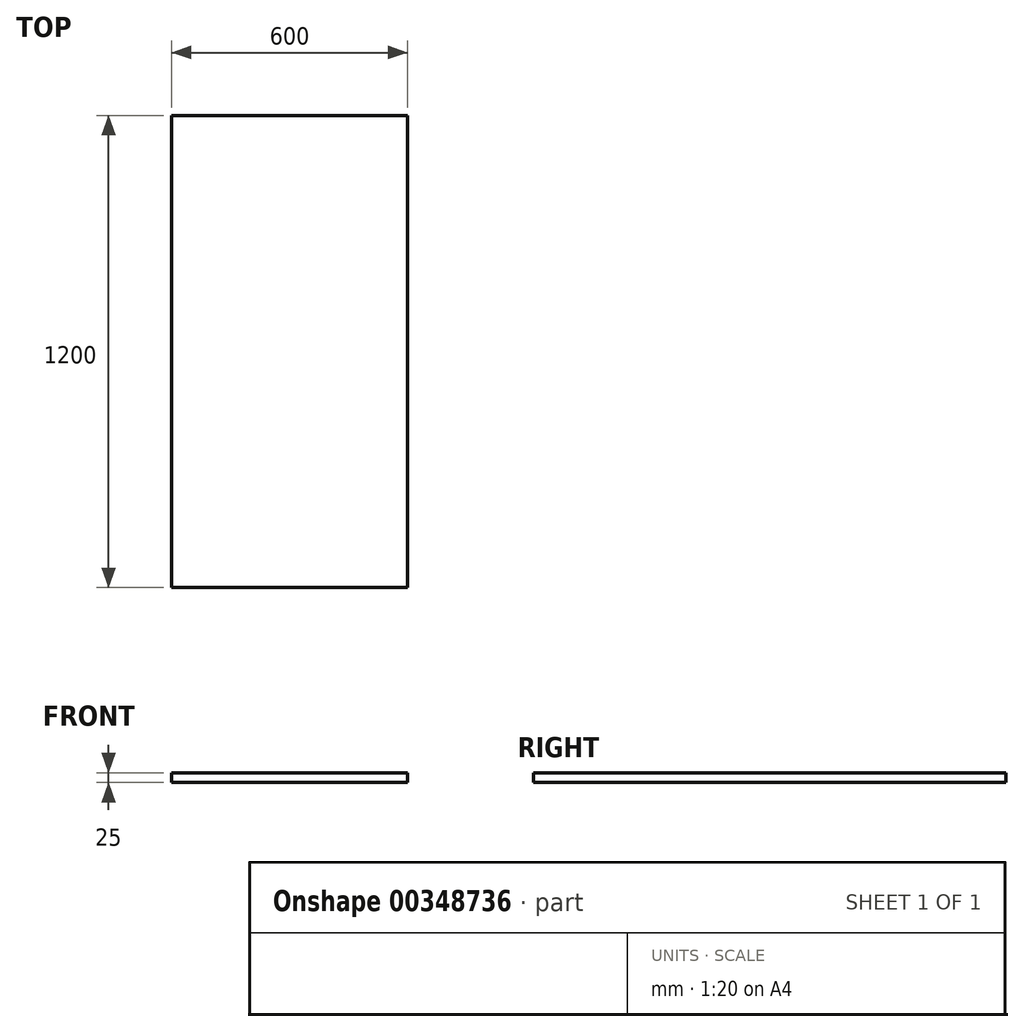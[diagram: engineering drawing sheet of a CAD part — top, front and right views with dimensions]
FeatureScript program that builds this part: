
annotation { "Feature Type Name" : "Feature", "Feature Type Description" : "" }
export const myFeature = defineFeature(function(context is Context, id is Id, definition is map)
    precondition{}
    {
        {
            var Q0;
            Q0=qCreatedBy(makeId("Top.planeOp"),FACE);
            var sketch = newSketch(context, id + "F0", { "sketchPlane" : qUnion([Q0])});
            skLineSegment(sketch, "E0.bottom", {"start": v(-48.19, 1086.35) * mm, "end": v(551.81, 1086.35) * mm});
            skLineSegment(sketch, "E0.top", {"start": v(-48.19, -113.65) * mm, "end": v(551.81, -113.65) * mm});
            skLineSegment(sketch, "E0.left", {"start": v(-48.19, 1086.35) * mm, "end": v(-48.19, -113.65) * mm});
            skLineSegment(sketch, "E0.right", {"start": v(551.81, 1086.35) * mm, "end": v(551.81, -113.65) * mm});
            skPoint(sketch, "E0.middle", {"position": v(251.81, 486.35) * mm});
            skSolve(sketch);
        }
        {
            var Q0;
            Q0=makeQuery(id+"F0.imprint","IMPRINT",FACE,{"disambiguationData":[TD([[makeQuery(id+"F0.imprint","IMPRINT",EDGE,{"derivedFrom":sQuery(id+"F0.wireOp",EDGE,"E0.bottom")}),-1.0]])]});
            extrude(context, id + "F1", {"entities" : qUnion([Q0]), "depth" : 25 * mm});
        }
    });
